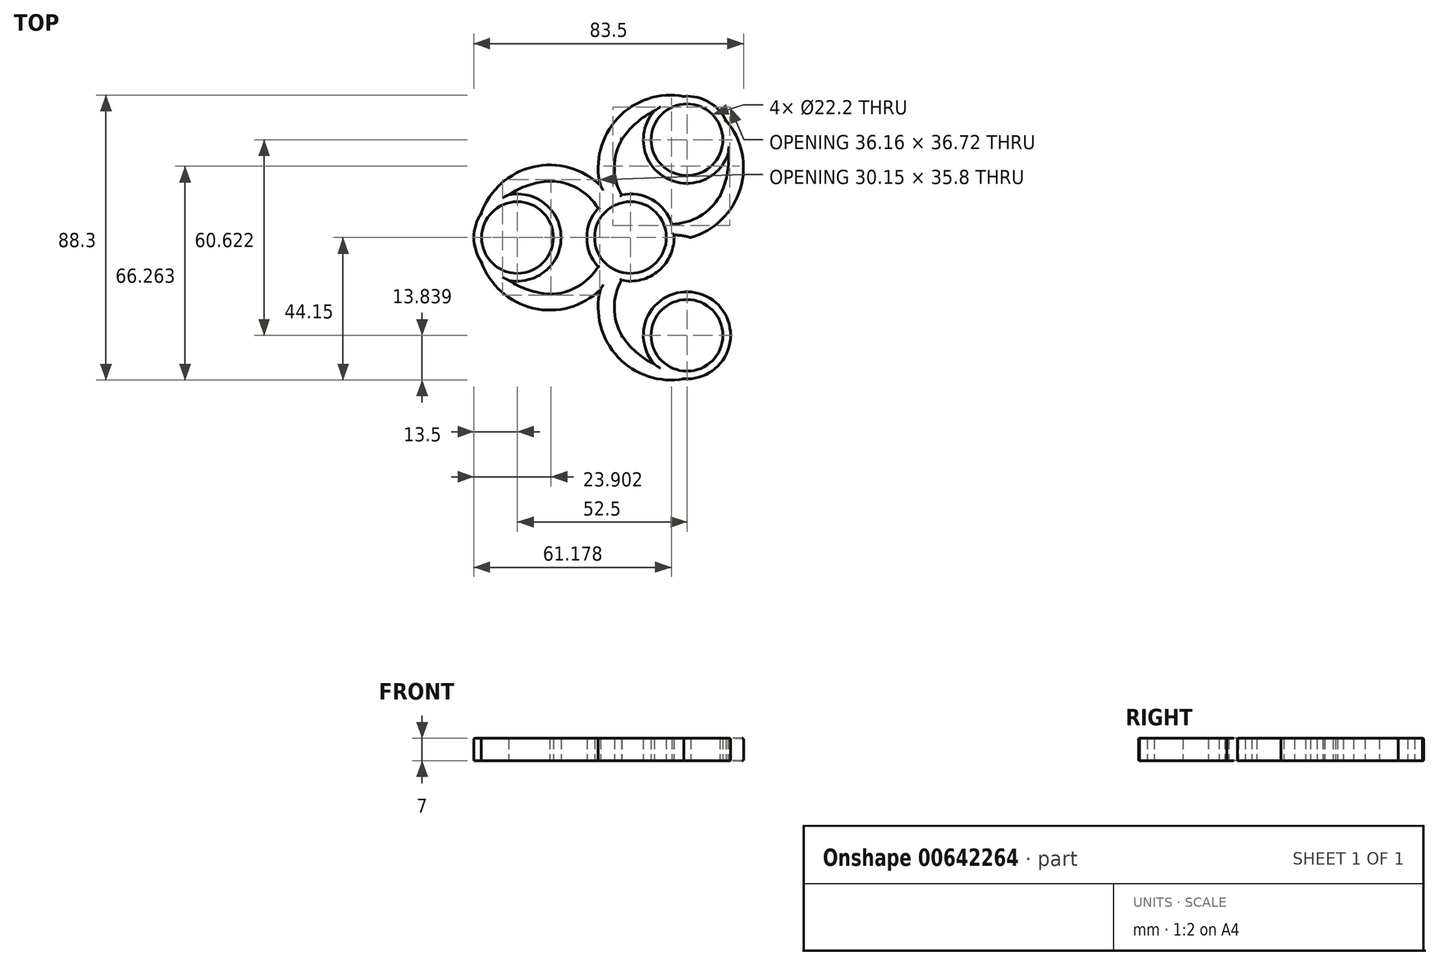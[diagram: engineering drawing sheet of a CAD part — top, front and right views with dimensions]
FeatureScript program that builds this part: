
annotation { "Feature Type Name" : "Feature", "Feature Type Description" : "" }
export const myFeature = defineFeature(function(context is Context, id is Id, definition is map)
    precondition{}
    {
        {
            var Q0;
            Q0=qCreatedBy(makeId("Top.planeOp"),FACE);
            var sketch = newSketch(context, id + "F0", { "sketchPlane" : qUnion([Q0])});
            skCircle(sketch, "E0", {"center": v(0, 0) * mm, "radius": 11.1 * mm});
            skCircle(sketch, "E1", {"center": v(0, 0) * mm, "radius": 13.5 * mm});
            skLineSegment(sketch, "E2", {"start": v(0, 0) * mm, "end": v(-35, 0) * mm, "construction": true});
            skCircle(sketch, "E3", {"center": v(-35, 0) * mm, "radius": 11.1 * mm});
            skCircle(sketch, "E4", {"center": v(-35, 0) * mm, "radius": 13.5 * mm});
            skCircle(sketch, "E5.1.0", {"center": v(17.5, -30.31) * mm, "radius": 11.1 * mm});
            skCircle(sketch, "E5.1.1", {"center": v(17.5, -30.31) * mm, "radius": 13.5 * mm});
            skCircle(sketch, "E5.2.0", {"center": v(17.5, 30.31) * mm, "radius": 11.1 * mm});
            skCircle(sketch, "E5.2.1", {"center": v(17.5, 30.31) * mm, "radius": 13.5 * mm});
            skSolve(sketch);
        }
        {
            var Q0;
            Q0=qCreatedBy(makeId("Top.planeOp"),FACE);
            var sketch = newSketch(context, id + "F1", { "sketchPlane" : qUnion([Q0])});
            skLineSegment(sketch, "E6", {"start": v(0, 0) * mm, "end": v(-25, 0) * mm, "construction": true});
            skArc(sketch, "E7", {"start": v(-25, -17.5) * mm, "mid": v(-7.5, 0) * mm, "end": v(-25, 17.5) * mm});
            skCircle(sketch, "E8", {"center": v(-25, 0) * mm, "radius": 22.5 * mm});
            skLineSegment(sketch, "E9", {"start": v(-25, 0) * mm, "end": v(-25, 22.5) * mm, "construction": true});
            skLineSegment(sketch, "E10", {"start": v(-25, 0) * mm, "end": v(-25, -22.5) * mm, "construction": true});
            skLineSegment(sketch, "E11", {"start": v(-25, 0) * mm, "end": v(-47.5, 0) * mm, "construction": true});
            skArc(sketch, "E12", {"start": v(-25, 17.5) * mm, "mid": v(-38.99, 12.27) * mm, "end": v(-47.5, 0) * mm});
            skArc(sketch, "E13.MirrorCS", {"start": v(-25, -17.5) * mm, "mid": v(-38.99, -12.27) * mm, "end": v(-47.5, 0) * mm});
            skArc(sketch, "E14.1.0", {"start": v(27.66, -12.9) * mm, "mid": v(30.12, -27.63) * mm, "end": v(23.75, -41.14) * mm});
            skLineSegment(sketch, "E14.1.1", {"start": v(12.5, -21.65) * mm, "end": v(-6.99, -32.9) * mm, "construction": true});
            skArc(sketch, "E14.1.2", {"start": v(-2.66, -30.4) * mm, "mid": v(8.87, -39.9) * mm, "end": v(23.75, -41.14) * mm});
            skLineSegment(sketch, "E14.1.3", {"start": v(12.5, -21.65) * mm, "end": v(23.75, -41.14) * mm, "construction": true});
            skArc(sketch, "E14.1.4", {"start": v(27.66, -12.9) * mm, "mid": v(3.75, -6.5) * mm, "end": v(-2.66, -30.4) * mm});
            skArc(sketch, "E14.1.5", {"start": v(-9.31, -16.13) * mm, "mid": v(33.52, -29.66) * mm, "end": v(-7.45, -11.26) * mm});
            skLineSegment(sketch, "E14.1.6", {"start": v(12.5, -21.65) * mm, "end": v(31.99, -10.4) * mm, "construction": true});
            skArc(sketch, "E14.2.0", {"start": v(-2.66, 30.4) * mm, "mid": v(8.87, 39.9) * mm, "end": v(23.75, 41.14) * mm});
            skLineSegment(sketch, "E14.2.1", {"start": v(12.5, 21.65) * mm, "end": v(31.99, 10.4) * mm, "construction": true});
            skArc(sketch, "E14.2.2", {"start": v(27.66, 12.9) * mm, "mid": v(30.12, 27.63) * mm, "end": v(23.75, 41.14) * mm});
            skLineSegment(sketch, "E14.2.3", {"start": v(12.5, 21.65) * mm, "end": v(23.75, 41.14) * mm, "construction": true});
            skArc(sketch, "E14.2.4", {"start": v(-2.66, 30.4) * mm, "mid": v(3.75, 6.5) * mm, "end": v(27.66, 12.9) * mm});
            skArc(sketch, "E14.2.5", {"start": v(-7.45, 11.26) * mm, "mid": v(1.25, 2.17) * mm, "end": v(13.47, -0.83) * mm});
            skLineSegment(sketch, "E14.2.6", {"start": v(12.5, 21.65) * mm, "end": v(-6.99, 32.9) * mm, "construction": true});
            skPoint(sketch, "E14.center", {"position": v(0, 0) * mm});
            skCircle(sketch, "E15.0.0", {"center": v(0, 0) * mm, "radius": 13.5 * mm});
            skCircle(sketch, "E16.0.0", {"center": v(-35, 0) * mm, "radius": 13.5 * mm});
            skCircle(sketch, "E17.0.0", {"center": v(17.5, 30.31) * mm, "radius": 13.5 * mm});
            skCircle(sketch, "E18.0.0", {"center": v(17.5, -30.31) * mm, "radius": 13.5 * mm});
            skCircle(sketch, "E19.0", {"center": v(0, 0) * mm, "radius": 11.1 * mm});
            skArc(sketch, "E20.trimOffspring", {"start": v(18.62, 0) * mm, "mid": v(23.75, 41.14) * mm, "end": v(-9.31, 16.13) * mm});
            skSolve(sketch);
        }
        {
            var Q0;
            Q0=makeQuery(id+"F0.imprint","IMPRINT",FACE,{"disambiguationData":[TD([[makeQuery(id+"F0.imprint","IMPRINT",EDGE,{"derivedFrom":sQuery(id+"F0.wireOp",EDGE,"E0")}),-1.0]])]});
            extrude(context, id + "F2", {"entities" : qUnion([Q0]), "depth" : 7 * mm, "offsetDistance" : 25 * mm});
        }
        {
            var Q0;
            {var subQ5=sQuery(id+"F1.wireOp",EDGE,"E12");var subQ6=sQuery(id+"F1.wireOp",EDGE,"E7");var subQ7=makeQuery(id+"F1.imprint","INTERSECT",VERTEX,{"derivedFrom":[subQ6,subQ5]});Q0=makeQuery(id+"F1.imprint","IMPRINT",FACE,{"disambiguationData":[TD([[makeQuery(id+"F1.imprint","IMPRINT",EDGE,{"disambiguationData":[TD([[subQ7,1.0]])],"derivedFrom":subQ6}),-1.0]])]});}
            var Q1;
            {var subQ0=sQuery(id+"F1.wireOp",EDGE,"E13.MirrorCS");var subQ1=sQuery(id+"F1.wireOp",EDGE,"E7");var subQ2=makeQuery(id+"F1.imprint","INTERSECT",VERTEX,{"derivedFrom":[subQ1,subQ0]});Q1=makeQuery(id+"F1.imprint","IMPRINT",FACE,{"disambiguationData":[TD([[makeQuery(id+"F1.imprint","IMPRINT",EDGE,{"disambiguationData":[TD([[subQ2,-1.0]])],"derivedFrom":subQ1}),-1.0]])]});}
            var Q2;
            Q2=makeQuery(id+"F0.imprint","IMPRINT",FACE,{"disambiguationData":[TD([[makeQuery(id+"F0.imprint","IMPRINT",EDGE,{"derivedFrom":sQuery(id+"F0.wireOp",EDGE,"E3")}),-1.0]])]});
            var Q3;
            {var subQ1=sQuery(id+"F1.wireOp",EDGE,"E8");var subQ9=sQuery(id+"F1.wireOp",EDGE,"E20.trimOffspring");var subQ10=makeQuery(id+"F1.imprint","INTERSECT",VERTEX,{"derivedFrom":[subQ1,subQ9]});Q3=makeQuery(id+"F1.imprint","IMPRINT",FACE,{"disambiguationData":[TD([[makeQuery(id+"F1.imprint","IMPRINT",EDGE,{"disambiguationData":[TD([[subQ10,1.0]])],"derivedFrom":subQ1}),-1.0]])]});}
            var Q4;
            {var subQ5=sQuery(id+"F1.wireOp",EDGE,"E20.trimOffspring");var subQ9=sQuery(id+"F1.wireOp",EDGE,"E14.1.5");var subQ11=makeQuery(id+"F1.imprint","INTERSECT",VERTEX,{"derivedFrom":[subQ9,subQ5]});Q4=makeQuery(id+"F1.imprint","IMPRINT",FACE,{"disambiguationData":[TD([[makeQuery(id+"F1.imprint","IMPRINT",EDGE,{"disambiguationData":[TD([[subQ11,-1.0]])],"derivedFrom":subQ9}),-1.0]])]});}
            var Q5;
            Q5=makeQuery(id+"F0.imprint","IMPRINT",FACE,{"disambiguationData":[TD([[makeQuery(id+"F0.imprint","IMPRINT",EDGE,{"derivedFrom":sQuery(id+"F0.wireOp",EDGE,"E5.2.0")}),-1.0]])]});
            var Q6;
            {var subQ6=sQuery(id+"F1.wireOp",EDGE,"E14.1.4");var subQ7=sQuery(id+"F1.wireOp",EDGE,"E14.1.0");var subQ8=makeQuery(id+"F1.imprint","INTERSECT",VERTEX,{"derivedFrom":[subQ7,subQ6]});Q6=makeQuery(id+"F1.imprint","IMPRINT",FACE,{"disambiguationData":[TD([[makeQuery(id+"F1.imprint","IMPRINT",EDGE,{"disambiguationData":[TD([[subQ8,-1.0]])],"derivedFrom":subQ7}),1.0]])]});}
            var Q7;
            {var subQ0=sQuery(id+"F1.wireOp",EDGE,"E14.1.5");var subQ1=sQuery(id+"F1.wireOp",EDGE,"E8");var subQ2=makeQuery(id+"F1.imprint","INTERSECT",VERTEX,{"disambiguationData":[OD(0.0)],"derivedFrom":[subQ1,subQ0]});Q7=makeQuery(id+"F1.imprint","IMPRINT",FACE,{"disambiguationData":[TD([[makeQuery(id+"F1.imprint","IMPRINT",EDGE,{"disambiguationData":[TD([[subQ2,-1.0]])],"derivedFrom":subQ1}),-1.0]])]});}
            var Q8;
            Q8=makeQuery(id+"F0.imprint","IMPRINT",FACE,{"disambiguationData":[TD([[makeQuery(id+"F0.imprint","IMPRINT",EDGE,{"derivedFrom":sQuery(id+"F0.wireOp",EDGE,"E5.1.0")}),-1.0]])]});
            extrude(context, id + "F3", {"entities" : qUnion([Q0, Q1, Q2, Q3, Q4, Q5, Q6, Q7, Q8]), "operationType" : NewBodyOperationType.ADD, "depth" : 7 * mm, "offsetDistance" : 25 * mm});
        }
        {
            var Q0;
            {var subQ0=sQuery(id+"F1.wireOp",EDGE,"E20.trimOffspring");var subQ1=sQuery(id+"F1.wireOp",EDGE,"E18.0.0");var subQ2=sQuery(id+"F1.wireOp",EDGE,"E17.0.0");var subQ3=sQuery(id+"F1.wireOp",EDGE,"E15.0.0");var subQ4=sQuery(id+"F1.wireOp",EDGE,"E14.2.4");var subQ5=sQuery(id+"F1.wireOp",EDGE,"E14.1.5");var subQ6=sQuery(id+"F1.wireOp",EDGE,"E14.1.4");var subQ7=sQuery(id+"F1.wireOp",EDGE,"E16.0.0");var subQ8=sQuery(id+"F1.wireOp",EDGE,"E8");var subQ9=sQuery(id+"F1.wireOp",EDGE,"E7");Q0=makeQuery(id+"F3.boolean.opBoolean","MERGE",FACE,{"derivedFrom":[makeQuery(id+"F2.opExtrude","CAP_FACE",FACE,{"disambiguationData":[OSD([sQuery(id+"F0.wireOp",EDGE,"E0"),sQuery(id+"F0.wireOp",EDGE,"E1")])],"isStart":false}),makeQuery(id+"F3.opExtrude","CAP_FACE",FACE,{"disambiguationData":[OSD([sQuery(id+"F0.wireOp",EDGE,"E3"),sQuery(id+"F0.wireOp",EDGE,"E4")])],"isStart":false}),makeQuery(id+"F3.opExtrude","CAP_FACE",FACE,{"disambiguationData":[OSD([sQuery(id+"F0.wireOp",EDGE,"E5.1.0"),sQuery(id+"F0.wireOp",EDGE,"E5.1.1")])],"isStart":false}),makeQuery(id+"F3.opExtrude","CAP_FACE",FACE,{"disambiguationData":[OSD([sQuery(id+"F0.wireOp",EDGE,"E5.2.0"),sQuery(id+"F0.wireOp",EDGE,"E5.2.1")])],"isStart":false}),makeQuery(id+"F3.opExtrude","CAP_FACE",FACE,{"disambiguationData":[OSD([subQ9,subQ8,sQuery(id+"F1.wireOp",EDGE,"E13.MirrorCS"),sQuery(id+"F1.wireOp",EDGE,"E14.1.2"),subQ6,subQ5,subQ3,subQ7,subQ1])],"isStart":false}),makeQuery(id+"F3.opExtrude","CAP_FACE",FACE,{"disambiguationData":[OSD([subQ9,subQ8,sQuery(id+"F1.wireOp",EDGE,"E12"),sQuery(id+"F1.wireOp",EDGE,"E14.2.0"),subQ4,subQ3,subQ7,subQ2,subQ0])],"isStart":false}),makeQuery(id+"F3.opExtrude","CAP_FACE",FACE,{"disambiguationData":[OSD([sQuery(id+"F1.wireOp",EDGE,"E14.1.0"),subQ6,subQ5,sQuery(id+"F1.wireOp",EDGE,"E14.2.2"),subQ4,subQ3,subQ2,subQ1,subQ0])],"isStart":false})]});}
            var Q1;
            {var subQ0=sQuery(id+"F1.wireOp",EDGE,"E8");Q1=makeQuery(id+"F3.opExtrude","CAP_EDGE",EDGE,{"disambiguationData":[OSD([subQ0]),TDD([makeQuery(id+"F1.imprint","IMPRINT",EDGE,{"disambiguationData":[TD([[makeQuery(id+"F1.imprint","INTERSECT",VERTEX,{"disambiguationData":[OD(0.0)],"derivedFrom":[subQ0,sQuery(id+"F1.wireOp",EDGE,"E14.1.5")]}),1.0]])],"derivedFrom":subQ0})])],"isStart":true});}
            var Q2;
            {var subQ0=sQuery(id+"F0.wireOp",EDGE,"E4");var subQ1=sQuery(id+"F1.wireOp",EDGE,"E20.trimOffspring");var subQ9=sQuery(id+"F1.wireOp",EDGE,"E8");Q2=makeQuery(id+"F3.boolean.opBoolean","SPLIT",EDGE,{"disambiguationData":[TD([makeQuery(id+"F3.opExtrude","SWEPT_FACE",FACE,{"disambiguationData":[OSD([subQ9]),TDD([makeQuery(id+"F1.imprint","IMPRINT",EDGE,{"disambiguationData":[TD([[makeQuery(id+"F1.imprint","INTERSECT",VERTEX,{"derivedFrom":[subQ9,subQ1]}),-1.0]])],"derivedFrom":subQ9})])]})])],"derivedFrom":makeQuery(id+"F3.opExtrude","CAP_EDGE",EDGE,{"disambiguationData":[OSD([subQ0])],"isStart":true})});}
            var Q3;
            {var subQ0=sQuery(id+"F1.wireOp",EDGE,"E8");Q3=makeQuery(id+"F3.opExtrude","CAP_EDGE",EDGE,{"disambiguationData":[OSD([subQ0]),TDD([makeQuery(id+"F1.imprint","IMPRINT",EDGE,{"disambiguationData":[TD([[makeQuery(id+"F1.imprint","INTERSECT",VERTEX,{"derivedFrom":[subQ0,sQuery(id+"F1.wireOp",EDGE,"E20.trimOffspring")]}),-1.0]])],"derivedFrom":subQ0})])],"isStart":true});}
            var Q4;
            {var subQ0=sQuery(id+"F1.wireOp",EDGE,"E20.trimOffspring");Q4=makeQuery(id+"F3.opExtrude","CAP_EDGE",EDGE,{"disambiguationData":[OSD([subQ0]),TDD([makeQuery(id+"F1.imprint","IMPRINT",EDGE,{"disambiguationData":[TD([[makeQuery(id+"F1.imprint","INTERSECT",VERTEX,{"derivedFrom":[sQuery(id+"F1.wireOp",EDGE,"E8"),subQ0]}),1.0]])],"derivedFrom":subQ0})])],"isStart":true});}
            var Q5;
            {var subQ0=sQuery(id+"F0.wireOp",EDGE,"E5.2.1");var subQ1=sQuery(id+"F1.wireOp",EDGE,"E20.trimOffspring");var subQ6=sQuery(id+"F1.wireOp",EDGE,"E14.1.5");Q5=makeQuery(id+"F3.boolean.opBoolean","SPLIT",EDGE,{"disambiguationData":[TD([makeQuery(id+"F3.opExtrude","SWEPT_FACE",FACE,{"disambiguationData":[OSD([subQ1]),TDD([makeQuery(id+"F1.imprint","IMPRINT",EDGE,{"disambiguationData":[TD([[makeQuery(id+"F1.imprint","INTERSECT",VERTEX,{"derivedFrom":[subQ6,subQ1]}),-1.0]])],"derivedFrom":subQ1})])]})])],"derivedFrom":makeQuery(id+"F3.opExtrude","CAP_EDGE",EDGE,{"disambiguationData":[OSD([subQ0])],"isStart":true})});}
            var Q6;
            Q6=makeQuery(id+"F3.opExtrude","CAP_EDGE",EDGE,{"disambiguationData":[OSD([sQuery(id+"F1.wireOp",EDGE,"E14.2.2")])],"isStart":true});
            var Q7;
            Q7=makeQuery(id+"F3.opExtrude","CAP_EDGE",EDGE,{"disambiguationData":[OSD([sQuery(id+"F1.wireOp",EDGE,"E14.2.0")])],"isStart":true});
            var Q8;
            {var subQ0=sQuery(id+"F1.wireOp",EDGE,"E13.MirrorCS");var subQ1=sQuery(id+"F1.wireOp",EDGE,"E7");var subQ9=sQuery(id+"F0.wireOp",EDGE,"E1");Q8=makeQuery(id+"F3.boolean.opBoolean","SPLIT",EDGE,{"disambiguationData":[TD([makeQuery(id+"F3.opExtrude","SWEPT_FACE",FACE,{"disambiguationData":[OSD([subQ1]),TDD([makeQuery(id+"F1.imprint","IMPRINT",EDGE,{"disambiguationData":[TD([[makeQuery(id+"F1.imprint","INTERSECT",VERTEX,{"derivedFrom":[subQ1,subQ0]}),-1.0]])],"derivedFrom":subQ1})])]})])],"derivedFrom":makeQuery(id+"F2.opExtrude","CAP_EDGE",EDGE,{"disambiguationData":[OSD([subQ9])],"isStart":true})});}
            var Q9;
            {var subQ4=sQuery(id+"F1.wireOp",EDGE,"E14.2.4");var subQ8=sQuery(id+"F0.wireOp",EDGE,"E1");var subQ9=sQuery(id+"F1.wireOp",EDGE,"E14.2.0");Q9=makeQuery(id+"F3.boolean.opBoolean","SPLIT",EDGE,{"disambiguationData":[TD([makeQuery(id+"F3.opExtrude","SWEPT_FACE",FACE,{"disambiguationData":[OSD([subQ4]),TDD([makeQuery(id+"F1.imprint","IMPRINT",EDGE,{"disambiguationData":[TD([[makeQuery(id+"F1.imprint","INTERSECT",VERTEX,{"derivedFrom":[subQ9,subQ4]}),-1.0]])],"derivedFrom":subQ4})])]})])],"derivedFrom":makeQuery(id+"F2.opExtrude","CAP_EDGE",EDGE,{"disambiguationData":[OSD([subQ8])],"isStart":true})});}
            var Q10;
            {var subQ0=sQuery(id+"F1.wireOp",EDGE,"E7");Q10=makeQuery(id+"F3.opExtrude","CAP_EDGE",EDGE,{"disambiguationData":[OSD([subQ0]),TDD([makeQuery(id+"F1.imprint","IMPRINT",EDGE,{"disambiguationData":[TD([[makeQuery(id+"F1.imprint","INTERSECT",VERTEX,{"derivedFrom":[subQ0,sQuery(id+"F1.wireOp",EDGE,"E13.MirrorCS")]}),-1.0]])],"derivedFrom":subQ0})])],"isStart":true});}
            var Q11;
            Q11=makeQuery(id+"F3.opExtrude","CAP_EDGE",EDGE,{"disambiguationData":[OSD([sQuery(id+"F1.wireOp",EDGE,"E13.MirrorCS")])],"isStart":true});
            var Q12;
            {var subQ0=sQuery(id+"F0.wireOp",EDGE,"E4");var subQ9=sQuery(id+"F1.wireOp",EDGE,"E12");Q12=makeQuery(id+"F3.boolean.opBoolean","SPLIT",EDGE,{"disambiguationData":[TD([makeQuery(id+"F3.opExtrude","SWEPT_FACE",FACE,{"disambiguationData":[OSD([subQ9])]})])],"derivedFrom":makeQuery(id+"F3.opExtrude","CAP_EDGE",EDGE,{"disambiguationData":[OSD([subQ0])],"isStart":true})});}
            var Q13;
            {var subQ0=sQuery(id+"F1.wireOp",EDGE,"E7");Q13=makeQuery(id+"F3.opExtrude","CAP_EDGE",EDGE,{"disambiguationData":[OSD([subQ0]),TDD([makeQuery(id+"F1.imprint","IMPRINT",EDGE,{"disambiguationData":[TD([[makeQuery(id+"F1.imprint","INTERSECT",VERTEX,{"derivedFrom":[subQ0,sQuery(id+"F1.wireOp",EDGE,"E12")]}),1.0]])],"derivedFrom":subQ0})])],"isStart":true});}
            var Q14;
            Q14=makeQuery(id+"F3.opExtrude","CAP_EDGE",EDGE,{"disambiguationData":[OSD([sQuery(id+"F1.wireOp",EDGE,"E12")])],"isStart":true});
            var Q15;
            {var subQ0=sQuery(id+"F1.wireOp",EDGE,"E20.trimOffspring");Q15=makeQuery(id+"F3.opExtrude","CAP_EDGE",EDGE,{"disambiguationData":[OSD([subQ0]),TDD([makeQuery(id+"F1.imprint","IMPRINT",EDGE,{"disambiguationData":[TD([[makeQuery(id+"F1.imprint","INTERSECT",VERTEX,{"derivedFrom":[sQuery(id+"F1.wireOp",EDGE,"E14.1.5"),subQ0]}),-1.0]])],"derivedFrom":subQ0})])],"isStart":true});}
            var Q16;
            {var subQ0=sQuery(id+"F1.wireOp",EDGE,"E14.1.5");Q16=makeQuery(id+"F3.opExtrude","CAP_EDGE",EDGE,{"disambiguationData":[OSD([subQ0]),TDD([makeQuery(id+"F1.imprint","IMPRINT",EDGE,{"disambiguationData":[TD([[makeQuery(id+"F1.imprint","INTERSECT",VERTEX,{"derivedFrom":[subQ0,sQuery(id+"F1.wireOp",EDGE,"E20.trimOffspring")]}),1.0]])],"derivedFrom":subQ0})])],"isStart":true});}
            var Q17;
            {var subQ0=sQuery(id+"F1.wireOp",EDGE,"E14.1.4");Q17=makeQuery(id+"F3.opExtrude","CAP_EDGE",EDGE,{"disambiguationData":[OSD([subQ0]),TDD([makeQuery(id+"F1.imprint","IMPRINT",EDGE,{"disambiguationData":[TD([[makeQuery(id+"F1.imprint","INTERSECT",VERTEX,{"derivedFrom":[sQuery(id+"F1.wireOp",EDGE,"E14.1.2"),subQ0]}),1.0]])],"derivedFrom":subQ0})])],"isStart":true});}
            var Q18;
            Q18=makeQuery(id+"F3.opExtrude","CAP_EDGE",EDGE,{"disambiguationData":[OSD([sQuery(id+"F1.wireOp",EDGE,"E14.1.2")])],"isStart":true});
            var Q19;
            Q19=makeQuery(id+"F3.opExtrude","CAP_EDGE",EDGE,{"disambiguationData":[OSD([sQuery(id+"F1.wireOp",EDGE,"E14.1.0")])],"isStart":true});
            var Q20;
            {var subQ0=sQuery(id+"F1.wireOp",EDGE,"E14.1.4");Q20=makeQuery(id+"F3.opExtrude","CAP_EDGE",EDGE,{"disambiguationData":[OSD([subQ0]),TDD([makeQuery(id+"F1.imprint","IMPRINT",EDGE,{"disambiguationData":[TD([[makeQuery(id+"F1.imprint","INTERSECT",VERTEX,{"derivedFrom":[sQuery(id+"F1.wireOp",EDGE,"E14.1.0"),subQ0]}),-1.0]])],"derivedFrom":subQ0})])],"isStart":true});}
            var Q21;
            {var subQ0=sQuery(id+"F0.wireOp",EDGE,"E5.2.1");var subQ10=sQuery(id+"F1.wireOp",EDGE,"E14.2.0");Q21=makeQuery(id+"F3.boolean.opBoolean","SPLIT",EDGE,{"disambiguationData":[TD([makeQuery(id+"F3.opExtrude","SWEPT_FACE",FACE,{"disambiguationData":[OSD([subQ10])]})])],"derivedFrom":makeQuery(id+"F3.opExtrude","CAP_EDGE",EDGE,{"disambiguationData":[OSD([subQ0])],"isStart":true})});}
            var Q22;
            {var subQ0=sQuery(id+"F1.wireOp",EDGE,"E14.1.5");Q22=makeQuery(id+"F3.opExtrude","CAP_EDGE",EDGE,{"disambiguationData":[OSD([subQ0]),TDD([makeQuery(id+"F1.imprint","IMPRINT",EDGE,{"disambiguationData":[TD([[makeQuery(id+"F1.imprint","INTERSECT",VERTEX,{"disambiguationData":[OD(0.0)],"derivedFrom":[sQuery(id+"F1.wireOp",EDGE,"E8"),subQ0]}),-1.0]])],"derivedFrom":subQ0})])],"isStart":true});}
            var Q23;
            {var subQ0=sQuery(id+"F0.wireOp",EDGE,"E5.1.1");var subQ2=sQuery(id+"F1.wireOp",EDGE,"E14.1.5");var subQ9=sQuery(id+"F1.wireOp",EDGE,"E8");Q23=makeQuery(id+"F3.boolean.opBoolean","SPLIT",EDGE,{"disambiguationData":[TD([makeQuery(id+"F3.opExtrude","SWEPT_FACE",FACE,{"disambiguationData":[OSD([subQ2]),TDD([makeQuery(id+"F1.imprint","IMPRINT",EDGE,{"disambiguationData":[TD([[makeQuery(id+"F1.imprint","INTERSECT",VERTEX,{"disambiguationData":[OD(0.0)],"derivedFrom":[subQ9,subQ2]}),-1.0]])],"derivedFrom":subQ2})])]})])],"derivedFrom":makeQuery(id+"F3.opExtrude","CAP_EDGE",EDGE,{"disambiguationData":[OSD([subQ0])],"isStart":true})});}
            fillet(context, id + "F4", {"entities" : qUnion([Q0, Q1, Q2, Q3, Q4, Q5, Q6, Q7, Q8, Q9, Q10, Q11, Q12, Q13, Q14, Q15, Q16, Q17, Q18, Q19, Q20, Q21, Q22, Q23]), "radius" : .4 * mm, "tangentPropagation" : true, "allowEdgeOverflow" : false});
        }
    });
